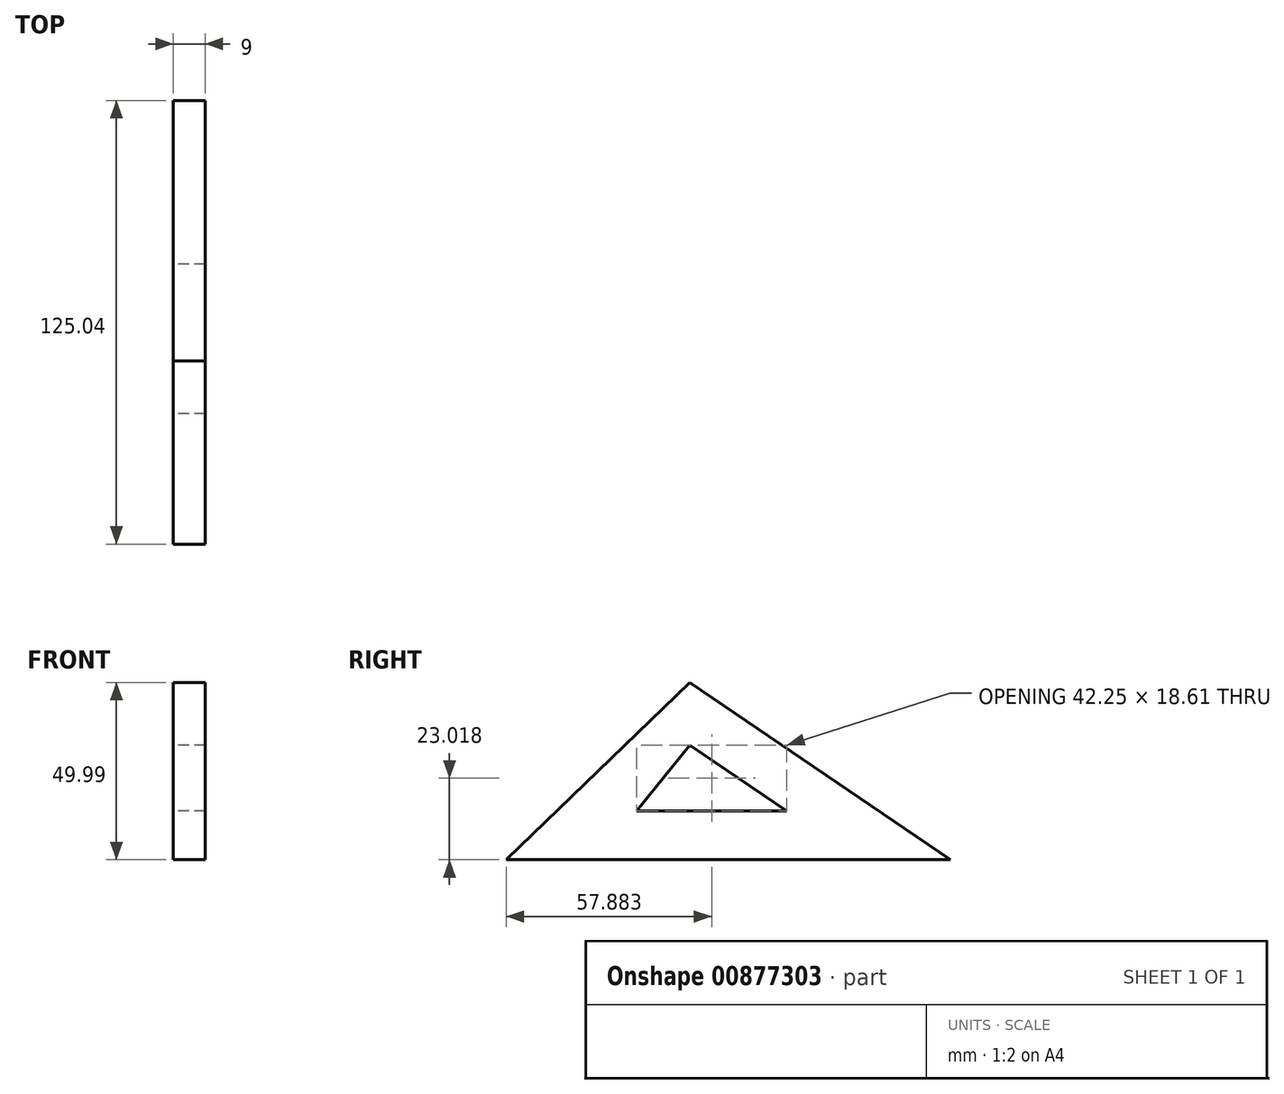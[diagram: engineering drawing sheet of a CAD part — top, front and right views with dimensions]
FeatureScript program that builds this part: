
annotation { "Feature Type Name" : "Feature", "Feature Type Description" : "" }
export const myFeature = defineFeature(function(context is Context, id is Id, definition is map)
    precondition{}
    {
        {
            var Q0;
            Q0=qCreatedBy(makeId("Right.planeOp"),FACE);
            var sketch = newSketch(context, id + "F0", { "sketchPlane" : qUnion([Q0])});
            skLineSegment(sketch, "E0", {"start": v(-51.7, 0) * mm, "end": v(0, 50) * mm});
            skLineSegment(sketch, "E1", {"start": v(0, 50) * mm, "end": v(73.33, 0) * mm});
            skLineSegment(sketch, "E2", {"start": v(73.33, 0) * mm, "end": v(-51.7, 0) * mm});
            skLineSegment(sketch, "E3", {"start": v(0, 32.32) * mm, "end": v(27.3, 13.71) * mm});
            skLineSegment(sketch, "E4", {"start": v(27.3, 13.71) * mm, "end": v(-14.95, 13.71) * mm});
            skLineSegment(sketch, "E5", {"start": v(-14.95, 13.71) * mm, "end": v(0, 32.32) * mm});
            skSolve(sketch);
        }
        {
            var Q0;
            Q0=makeQuery(id+"F0.imprint","IMPRINT",FACE,{"disambiguationData":[TD([[makeQuery(id+"F0.imprint","IMPRINT",EDGE,{"derivedFrom":sQuery(id+"F0.wireOp",EDGE,"E0")}),-1.0]])]});
            extrude(context, id + "F1", {"entities" : qUnion([Q0]), "depth" : 9 * mm, "offsetDistance" : 25 * mm});
        }
    });
